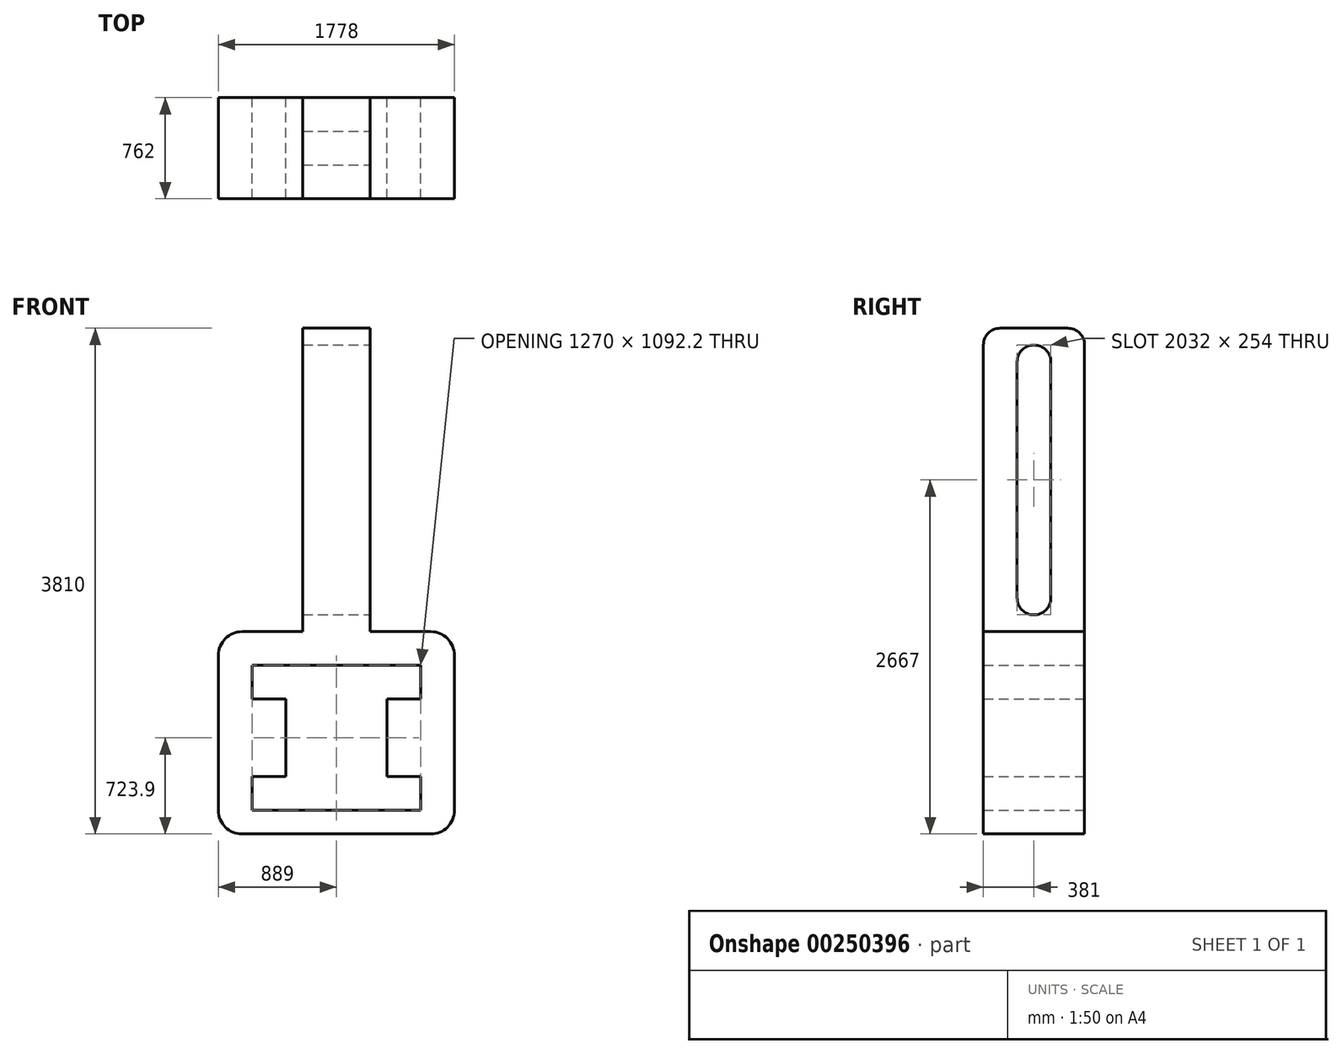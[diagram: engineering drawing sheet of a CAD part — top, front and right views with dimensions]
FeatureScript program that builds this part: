
annotation { "Feature Type Name" : "Feature", "Feature Type Description" : "" }
export const myFeature = defineFeature(function(context is Context, id is Id, definition is map)
    precondition{}
    {
        {
            var Q0;
            Q0=qCreatedBy(makeId("Front.planeOp"),FACE);
            var sketch = newSketch(context, id + "F0", { "sketchPlane" : qUnion([Q0])});
            skLineSegment(sketch, "E0.bottom", {"start": v(-711.2, 762) * mm, "end": v(711.2, 762) * mm});
            skLineSegment(sketch, "E0.top", {"start": v(-711.2, -762) * mm, "end": v(711.2, -762) * mm});
            skLineSegment(sketch, "E0.left", {"start": v(-889, 584.2) * mm, "end": v(-889, -584.2) * mm});
            skLineSegment(sketch, "E0.right", {"start": v(889, 584.2) * mm, "end": v(889, -584.2) * mm});
            skPoint(sketch, "E0.middle", {"position": v(0, 0) * mm});
            skPoint(sketch, "E1.visualSharp", {"position": v(-889, 762) * mm});
            skArc(sketch, "E1.filletArc", {"start": v(-711.2, 762) * mm, "mid": v(-836.92, 709.92) * mm, "end": v(-889, 584.2) * mm});
            skPoint(sketch, "E2.visualSharp", {"position": v(889, 762) * mm});
            skArc(sketch, "E2.filletArc", {"start": v(889, 584.2) * mm, "mid": v(836.92, 709.92) * mm, "end": v(711.2, 762) * mm});
            skPoint(sketch, "E3.visualSharp", {"position": v(889, -762) * mm});
            skArc(sketch, "E3.filletArc", {"start": v(711.2, -762) * mm, "mid": v(836.92, -709.92) * mm, "end": v(889, -584.2) * mm});
            skPoint(sketch, "E4.visualSharp", {"position": v(-889, -762) * mm});
            skArc(sketch, "E4.filletArc", {"start": v(-889, -584.2) * mm, "mid": v(-836.92, -709.92) * mm, "end": v(-711.2, -762) * mm});
            skLineSegment(sketch, "E5", {"start": v(-635, -584.2) * mm, "end": v(635, -584.2) * mm});
            skLineSegment(sketch, "E6", {"start": v(635, -584.2) * mm, "end": v(635, -330.2) * mm});
            skLineSegment(sketch, "E7", {"start": v(635, -330.2) * mm, "end": v(381, -330.2) * mm});
            skLineSegment(sketch, "E8", {"start": v(381, -330.2) * mm, "end": v(381, 177.8) * mm});
            skLineSegment(sketch, "E9", {"start": v(-381, 177.8) * mm, "end": v(-381, -330.2) * mm});
            skLineSegment(sketch, "E10", {"start": v(-381, -330.2) * mm, "end": v(-635, -330.2) * mm});
            skLineSegment(sketch, "E11", {"start": v(-635, -330.2) * mm, "end": v(-635, -584.2) * mm});
            skLineSegment(sketch, "E12", {"start": v(-635, 508) * mm, "end": v(635, 508) * mm});
            skLineSegment(sketch, "E13", {"start": v(635, 508) * mm, "end": v(635, 254) * mm});
            skLineSegment(sketch, "E14", {"start": v(635, 254) * mm, "end": v(381, 254) * mm});
            skLineSegment(sketch, "E15", {"start": v(381, 254) * mm, "end": v(381, 177.8) * mm});
            skLineSegment(sketch, "E16", {"start": v(-635, 508) * mm, "end": v(-635, 254) * mm});
            skLineSegment(sketch, "E17", {"start": v(-635, 254) * mm, "end": v(-381, 254) * mm});
            skLineSegment(sketch, "E18", {"start": v(-381, 254) * mm, "end": v(-381, 177.8) * mm});
            skSolve(sketch);
        }
        {
            var Q0;
            Q0=makeQuery(id+"F0.imprint","IMPRINT",FACE,{"disambiguationData":[TD([[makeQuery(id+"F0.imprint","IMPRINT",EDGE,{"derivedFrom":sQuery(id+"F0.wireOp",EDGE,"E0.bottom")}),-1.0]])]});
            extrude(context, id + "F1", {"entities" : qUnion([Q0]), "depth" : 762 * mm});
        }
        {
            var Q0;
            Q0=makeQuery(id+"F1.opExtrude","SWEPT_FACE",FACE,{"disambiguationData":[OSD([sQuery(id+"F0.wireOp",EDGE,"E0.bottom")])]});
            var sketch = newSketch(context, id + "F2", { "sketchPlane" : qUnion([Q0])});
            skLineSegment(sketch, "E19", {"start": v(-254, 0) * mm, "end": v(-254, -762) * mm});
            skLineSegment(sketch, "E20", {"start": v(254, 0) * mm, "end": v(254, -762) * mm});
            skLineSegment(sketch, "E21", {"start": v(-254, -254) * mm, "end": v(254, -254) * mm, "construction": true});
            skLineSegment(sketch, "E22", {"start": v(-254, -508) * mm, "end": v(254, -508) * mm, "construction": true});
            skSolve(sketch);
        }
        {
            var Q0;
            {var subQ0=sQuery(id+"F2.wireOp",EDGE,"E19");Q0=makeQuery(id+"F2.imprint","IMPRINT",FACE,{"disambiguationData":[TD([[makeQuery(id+"F2.imprint","IMPRINT",EDGE,{"derivedFrom":subQ0}),1.0]])]});}
            extrude(context, id + "F3", {"entities" : qUnion([Q0]), "operationType" : NewBodyOperationType.ADD, "depth" : 2286 * mm});
        }
        {
            var Q0;
            {var subQ0=sQuery(id+"F0.wireOp",EDGE,"E0.bottom");var subQ1=makeQuery(id+"F1.opExtrude","CAP_EDGE",EDGE,{"disambiguationData":[OSD([subQ0])],"isStart":false});Q0=makeQuery(id+"F3.opExtrude","CAP_EDGE",EDGE,{"disambiguationData":[OSD([subQ0]),TDD([makeQuery(id+"F2.imprint","IMPRINT",EDGE,{"disambiguationData":[TD([[makeQuery(id+"F2.imprint","INTERSECT",VERTEX,{"derivedFrom":[subQ1,sQuery(id+"F2.wireOp",EDGE,"E19")]}),-1.0]])],"derivedFrom":subQ1})])],"isStart":false});}
            var Q1;
            {var subQ0=sQuery(id+"F0.wireOp",EDGE,"E0.bottom");var subQ1=makeQuery(id+"F1.opExtrude","CAP_EDGE",EDGE,{"disambiguationData":[OSD([subQ0])],"isStart":true});Q1=makeQuery(id+"F3.opExtrude","CAP_EDGE",EDGE,{"disambiguationData":[OSD([subQ0]),TDD([makeQuery(id+"F2.imprint","IMPRINT",EDGE,{"disambiguationData":[TD([[makeQuery(id+"F2.imprint","INTERSECT",VERTEX,{"derivedFrom":[subQ1,sQuery(id+"F2.wireOp",EDGE,"E19")]}),-1.0]])],"derivedFrom":subQ1})])],"isStart":false});}
            fillet(context, id + "F4", {"entities" : qUnion([Q0, Q1]), "radius" : 127 * mm, "tangentPropagation" : true, "allowEdgeOverflow" : false});
        }
        {
            var Q0;
            Q0=makeQuery(id+"F3.opExtrude","SWEPT_FACE",FACE,{"disambiguationData":[OSD([sQuery(id+"F2.wireOp",EDGE,"E20")])]});
            var sketch = newSketch(context, id + "F5", { "sketchPlane" : qUnion([Q0])});
            skLineSegment(sketch, "E23", {"start": v(-709.26, 976.69) * mm, "end": v(-683.86, 976.69) * mm});
            skLineSegment(sketch, "E24", {"start": v(-855.54, 1016) * mm, "end": v(277.42, 1016) * mm, "construction": true});
            skArc(sketch, "E25", {"start": v(-254, 2794) * mm, "mid": v(-381, 2921) * mm, "end": v(-508, 2794) * mm});
            skArc(sketch, "E26", {"start": v(-508, 1016) * mm, "mid": v(-381, 889) * mm, "end": v(-254, 1016) * mm});
            skLineSegment(sketch, "E27", {"start": v(-254, 2794) * mm, "end": v(-254, 1016) * mm});
            skLineSegment(sketch, "E28", {"start": v(-508, 2794) * mm, "end": v(-508, 1016) * mm});
            skLineSegment(sketch, "E29.trimOffspring", {"start": v(-381, 2794) * mm, "end": v(-381, 2921) * mm, "construction": true});
            skPoint(sketch, "E30.start.orphan", {"position": v(-381, 762) * mm});
            skSolve(sketch);
        }
        {
            var Q0;
            Q0=makeQuery(id+"F5.imprint","IMPRINT",FACE,{"disambiguationData":[TD([[makeQuery(id+"F5.imprint","IMPRINT",EDGE,{"derivedFrom":sQuery(id+"F5.wireOp",EDGE,"E25")}),1.0]])]});
            extrude(context, id + "F6", {"entities" : qUnion([Q0]), "oppositeDirection" : true, "depth" : 1648.46 * mm});
        }
        {
            var Q0;
            Q0=makeQuery(id+"F6.opExtrude","SWEPT_BODY",BODY,{"disambiguationData":[OSD([sQuery(id+"F5.wireOp",EDGE,"E25"),sQuery(id+"F5.wireOp",EDGE,"E26"),sQuery(id+"F5.wireOp",EDGE,"E27"),sQuery(id+"F5.wireOp",EDGE,"E28")])]});
            var Q1;
            Q1=makeQuery(id+"F1.opExtrude","SWEPT_BODY",BODY,{"disambiguationData":[OSD([sQuery(id+"F0.wireOp",EDGE,"E0.bottom"),sQuery(id+"F0.wireOp",EDGE,"E0.top"),sQuery(id+"F0.wireOp",EDGE,"E0.left"),sQuery(id+"F0.wireOp",EDGE,"E0.right"),sQuery(id+"F0.wireOp",EDGE,"E1.filletArc"),sQuery(id+"F0.wireOp",EDGE,"E2.filletArc"),sQuery(id+"F0.wireOp",EDGE,"E3.filletArc"),sQuery(id+"F0.wireOp",EDGE,"E4.filletArc"),sQuery(id+"F0.wireOp",EDGE,"E5"),sQuery(id+"F0.wireOp",EDGE,"E6"),sQuery(id+"F0.wireOp",EDGE,"E7"),sQuery(id+"F0.wireOp",EDGE,"E8"),sQuery(id+"F0.wireOp",EDGE,"E9"),sQuery(id+"F0.wireOp",EDGE,"E10"),sQuery(id+"F0.wireOp",EDGE,"E11"),sQuery(id+"F0.wireOp",EDGE,"E12"),sQuery(id+"F0.wireOp",EDGE,"E13"),sQuery(id+"F0.wireOp",EDGE,"E14"),sQuery(id+"F0.wireOp",EDGE,"E15"),sQuery(id+"F0.wireOp",EDGE,"E16"),sQuery(id+"F0.wireOp",EDGE,"E17"),sQuery(id+"F0.wireOp",EDGE,"E18")])]});
            booleanBodies(context, id + "F7", {"operationType" : BooleanOperationType.SUBTRACTION, "tools" : qUnion([Q0]), "targets" : qUnion([Q1])});
        }
    });
